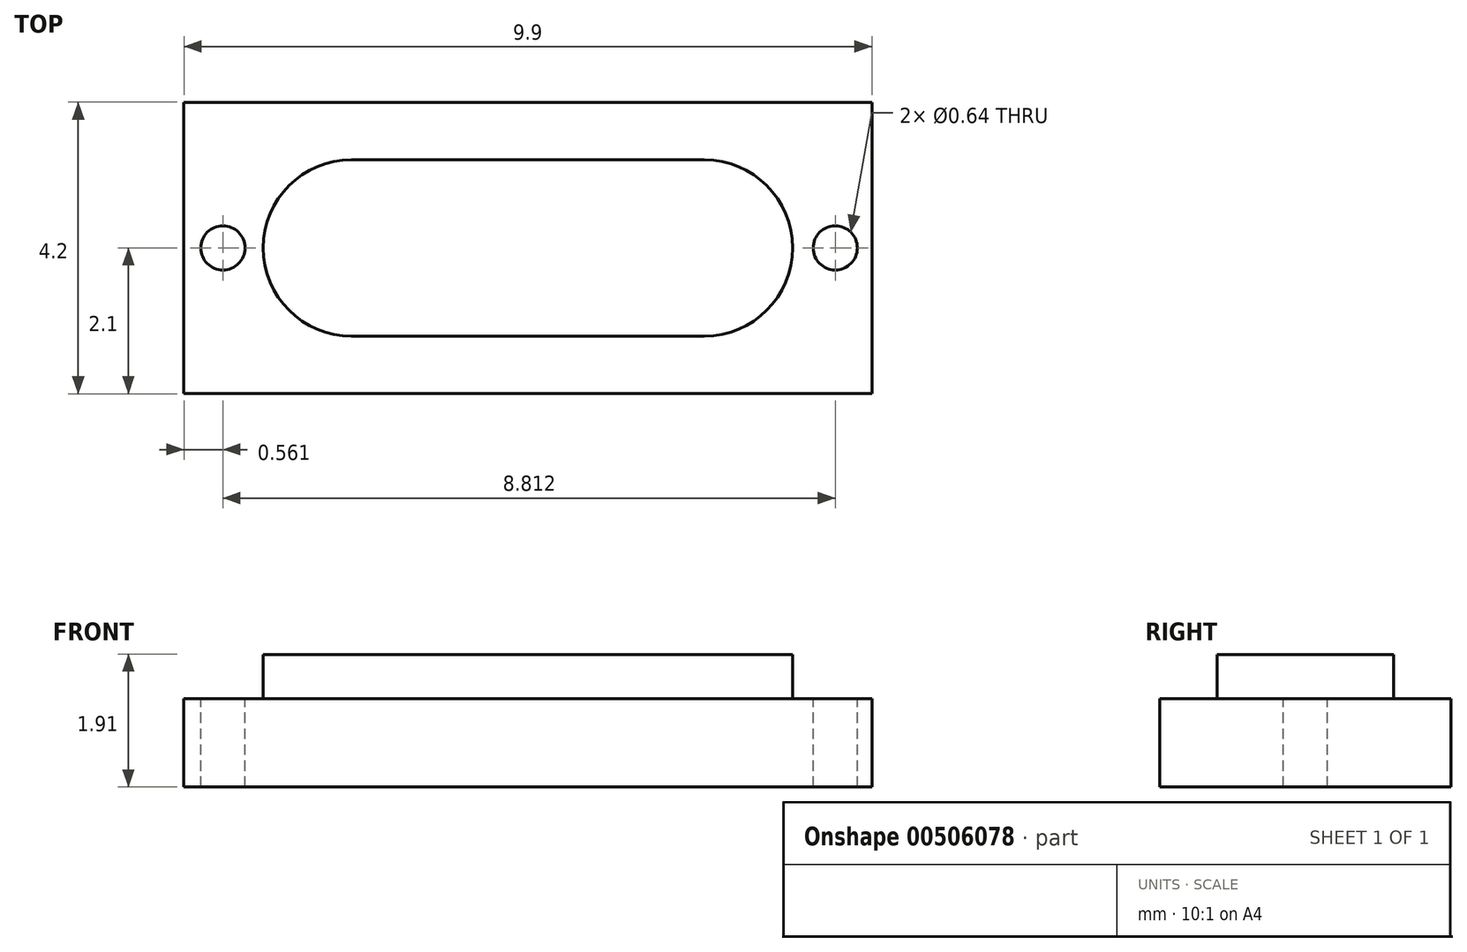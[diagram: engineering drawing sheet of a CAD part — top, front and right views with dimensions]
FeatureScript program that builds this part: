
annotation { "Feature Type Name" : "Feature", "Feature Type Description" : "" }
export const myFeature = defineFeature(function(context is Context, id is Id, definition is map)
    precondition{}
    {
        {
            var Q0;
            Q0=qCreatedBy(makeId("Top.planeOp"),FACE);
            var sketch = newSketch(context, id + "F0", { "sketchPlane" : qUnion([Q0])});
            skLineSegment(sketch, "E0.bottom", {"start": v(4.95, 2.1) * mm, "end": v(-4.95, 2.1) * mm});
            skLineSegment(sketch, "E0.top", {"start": v(4.95, -2.1) * mm, "end": v(-4.95, -2.1) * mm});
            skLineSegment(sketch, "E0.left", {"start": v(4.95, 2.1) * mm, "end": v(4.95, -2.1) * mm});
            skLineSegment(sketch, "E0.right", {"start": v(-4.95, 2.1) * mm, "end": v(-4.95, -2.1) * mm});
            skPoint(sketch, "E0.middle", {"position": v(0, 0) * mm});
            skSolve(sketch);
        }
        {
            var Q0;
            Q0=makeQuery(id+"F0.imprint","IMPRINT",FACE,{"disambiguationData":[TD([[makeQuery(id+"F0.imprint","IMPRINT",EDGE,{"derivedFrom":sQuery(id+"F0.wireOp",EDGE,"E0.bottom")}),1.0]])]});
            extrude(context, id + "F1", {"entities" : qUnion([Q0]), "depth" : 1.27 * mm});
        }
        {
            var Q0;
            Q0=makeQuery(id+"F1.opExtrude","CAP_FACE",FACE,{"disambiguationData":[OSD([sQuery(id+"F0.wireOp",EDGE,"E0.bottom"),sQuery(id+"F0.wireOp",EDGE,"E0.top"),sQuery(id+"F0.wireOp",EDGE,"E0.left"),sQuery(id+"F0.wireOp",EDGE,"E0.right")])],"isStart":false});
            var sketch = newSketch(context, id + "F2", { "sketchPlane" : qUnion([Q0])});
            skLineSegment(sketch, "E1.bottom", {"start": v(2.54, 1.27) * mm, "end": v(-2.54, 1.27) * mm});
            skLineSegment(sketch, "E1.top", {"start": v(2.54, -1.27) * mm, "end": v(-2.54, -1.27) * mm});
            skLineSegment(sketch, "E1.left", {"start": v(3.81, 0) * mm, "end": v(3.81, 0) * mm});
            skLineSegment(sketch, "E1.right", {"start": v(-3.81, 0) * mm, "end": v(-3.81, 0) * mm});
            skPoint(sketch, "E1.middle", {"position": v(0, 0) * mm});
            skPoint(sketch, "E2.visualSharp", {"position": v(-3.81, 1.27) * mm});
            skArc(sketch, "E2.filletArc", {"start": v(-2.54, 1.27) * mm, "mid": v(-3.44, 0.9) * mm, "end": v(-3.81, 0) * mm});
            skPoint(sketch, "E3.visualSharp", {"position": v(-3.81, -1.27) * mm});
            skArc(sketch, "E3.filletArc", {"start": v(-3.81, 0) * mm, "mid": v(-3.44, -0.9) * mm, "end": v(-2.54, -1.27) * mm});
            skPoint(sketch, "E4.visualSharp", {"position": v(3.81, 1.27) * mm});
            skArc(sketch, "E4.filletArc", {"start": v(3.81, 0) * mm, "mid": v(3.44, 0.9) * mm, "end": v(2.54, 1.27) * mm});
            skPoint(sketch, "E5.visualSharp", {"position": v(3.81, -1.27) * mm});
            skArc(sketch, "E5.filletArc", {"start": v(2.54, -1.27) * mm, "mid": v(3.44, -0.9) * mm, "end": v(3.81, 0) * mm});
            skSolve(sketch);
        }
        {
            var Q0;
            Q0=makeQuery(id+"F2.imprint","IMPRINT",FACE,{"disambiguationData":[TD([[makeQuery(id+"F2.imprint","IMPRINT",EDGE,{"derivedFrom":sQuery(id+"F2.wireOp",EDGE,"E1.bottom")}),1.0]])]});
            extrude(context, id + "F3", {"entities" : qUnion([Q0]), "operationType" : NewBodyOperationType.ADD, "depth" : 0.64 * mm});
        }
        {
            var Q0;
            Q0=makeQuery(id+"F1.opExtrude","CAP_FACE",FACE,{"disambiguationData":[OSD([sQuery(id+"F0.wireOp",EDGE,"E0.bottom"),sQuery(id+"F0.wireOp",EDGE,"E0.top"),sQuery(id+"F0.wireOp",EDGE,"E0.left"),sQuery(id+"F0.wireOp",EDGE,"E0.right")])],"isStart":false});
            var sketch = newSketch(context, id + "F4", { "sketchPlane" : qUnion([Q0])});
            skCircle(sketch, "E6", {"center": v(-4.39, 0) * mm, "radius": 0.32 * mm});
            skPoint(sketch, "E6.centerSnap0", {"position": v(-3.81, 0) * mm});
            skCircle(sketch, "E7", {"center": v(4.42, 0) * mm, "radius": 0.32 * mm});
            skSolve(sketch);
        }
        {
            var Q0;
            Q0=makeQuery(id+"F4.imprint","IMPRINT",FACE,{"disambiguationData":[TD([[makeQuery(id+"F4.imprint","IMPRINT",EDGE,{"derivedFrom":sQuery(id+"F4.wireOp",EDGE,"E7")}),1.0]])]});
            var Q1;
            Q1=makeQuery(id+"F4.imprint","IMPRINT",FACE,{"disambiguationData":[TD([[makeQuery(id+"F4.imprint","IMPRINT",EDGE,{"derivedFrom":sQuery(id+"F4.wireOp",EDGE,"E6")}),1.0]])]});
            extrude(context, id + "F5", {"entities" : qUnion([Q0, Q1]), "operationType" : NewBodyOperationType.REMOVE, "oppositeDirection" : true, "depth" : 25.4 * mm, "offsetDistance" : 25.4 * mm});
        }
    });
